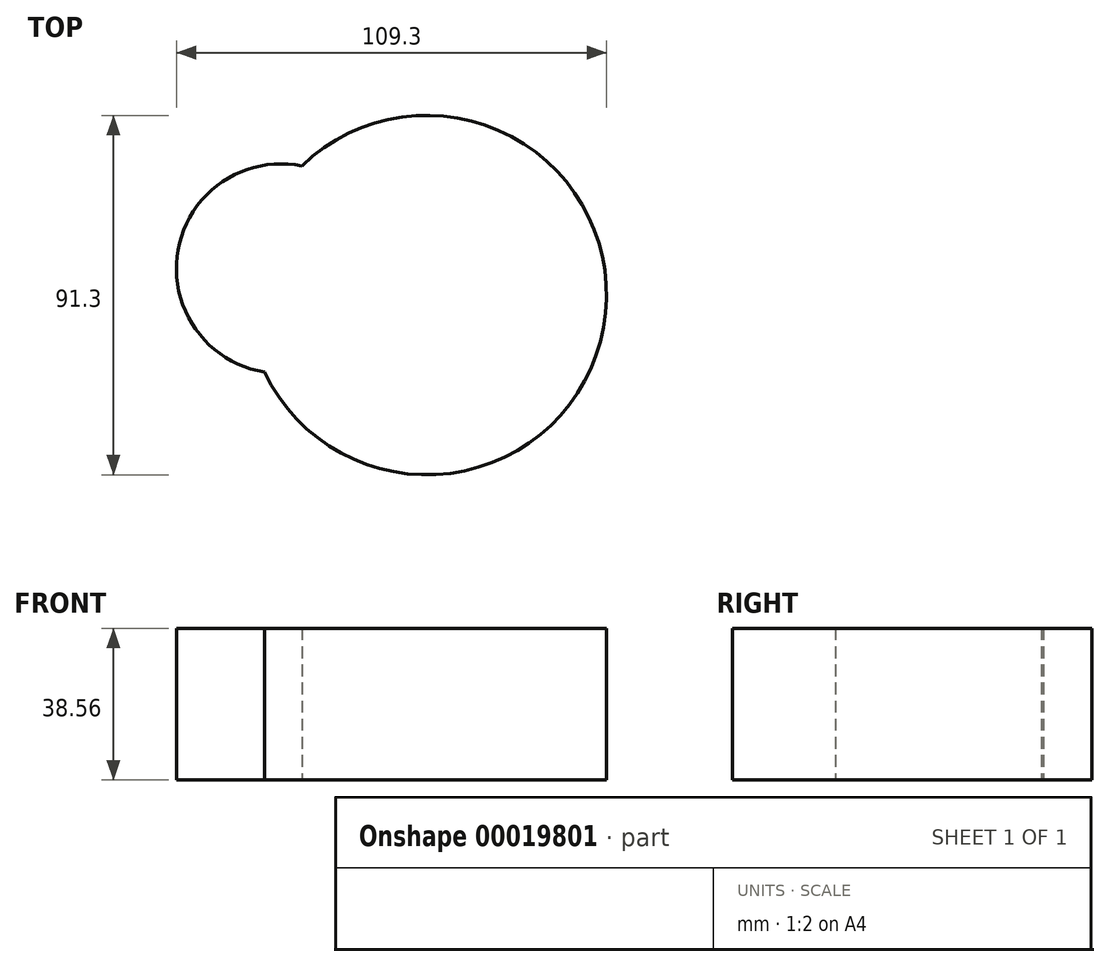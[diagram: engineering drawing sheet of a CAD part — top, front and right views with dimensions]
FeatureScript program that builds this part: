
annotation { "Feature Type Name" : "Feature", "Feature Type Description" : "" }
export const myFeature = defineFeature(function(context is Context, id is Id, definition is map)
    precondition{}
    {
        {
            var Q0;
            Q0=qCreatedBy(makeId("Top.planeOp"),FACE);
            var sketch = newSketch(context, id + "F0", { "sketchPlane" : qUnion([Q0])});
            skArc(sketch, "E0", {"start": v(-82.7, -4.14) * mm, "mid": v(-114.19, -25.46) * mm, "end": v(-92.24, -56.5) * mm});
            skArc(sketch, "E1", {"start": v(-92.24, -56.5) * mm, "mid": v(-6.06, -45.14) * mm, "end": v(-82.7, -4.14) * mm});
            skSolve(sketch);
        }
        {
            var Q0;
            Q0=makeQuery(id+"F0.imprint","IMPRINT",FACE,{"disambiguationData":[TD([[makeQuery(id+"F0.imprint","IMPRINT",EDGE,{"derivedFrom":sQuery(id+"F0.wireOp",EDGE,"E0")}),1.0]])]});
            extrude(context, id + "F1", {"entities" : qUnion([Q0]), "depth" : 38.56 * mm});
        }
    });
